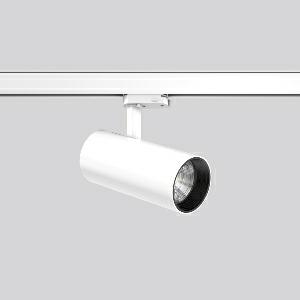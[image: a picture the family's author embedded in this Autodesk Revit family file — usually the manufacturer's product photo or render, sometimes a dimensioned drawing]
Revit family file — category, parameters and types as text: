
# Revit family: deecos_s_mini_742199_002_3_76_5bb7
name_source: partatom
category: Lighting Fixtures
units: mm (PartAtom-declared; Revit-internal decimal feet)

## family parameters
Cut with Voids When Loaded = No
Host = Face
Light Source = No
Part Type = Normal
Room Calculation Point = No
Round Connector Dimension = Use Diameter
Shared = No

## types (1)
- DEECOS S mini (1 x LED Modul 935, 2150 lm, 3500)
    Apparent Load = 20 VA
    Approval mark = CE
    CIE Flux Codes = 96 100 100 100 100
    Color Rendering = 92
    Color Temperature = 3500
    Default Elevation = 1800 mm
    Description = Series: DEECOS S mini
LED surface-mounted projector in modern design with no visible cooling ribs. Housing: die-cast aluminium, powder-coated. Rotation range: 356°. Swivel range: 90°. Black plastic ring and recessed LED to prevent glare from the side. Optical assembly with lens made of plastic (polycarbonate) for the best homogeneous light distribution - can be changed without tools. Best colour rendering index Ra>90. With adapter for RZB 3-circuit DALI tracks. Suitable for Track on ceiling, Wall track. High quality converter without flickering and stroboscopic effect. The following accessories can be mounted without use of tools: interchangeable lenses, decorative glasses, honeycomb louvre, clear and frosted diffusers, white interchangeable plastic ring. 
Colour: traffic white, matt (RAL 9016)
Diameter: 87 mm
Height: 214 mm
Lamp: LED
Socket: without socket
Colour temperature: 3500K
Colour rendering index (CRI): 92
System power: 20 W
Rated luminous flux: 2150 lm
Luminous efficiency: 108 lm/W
Control gear: Converter, dimmable, DALI
Protection class: I
Type of protection: IP 20
    Height = 214 mm
    Lamp = 1 x LED Modul 935
    Lamp Light Flux = 2150 lm
    Lamp count = 1
    Length = 87 mm
    Lifetime = 50000 h
    Luminous efficacy = 108 lm/W
    Manufacturer = RZB
    ModVariant = No
    Model = 742199.002.3.76
    Mounting Place = Ceiling
    Mounting Type = Rail mounted
    Number of Poles = 1
    OnlyDefault = Yes
    Power Factor = 1
    Product Name = DEECOS S mini
    Product group = Track mounted projectors
    ProductGroupID = 301
    Protection Class = Protection class I
    Protection Degree = IP 20
    RLX_Detail_Level = 1
    RLX_Emergency_Light_Flux = 0 lm
    RLX_Emergency_Type = 0
    RLX_Emergency_Type_DB = No
    RlxData = <blob elided: 35045 chars, md5=e0292836>
    Socket = socket
    Standby Power = 0 W
    System Light Flux = 2150 lm
    System Power = 20 W
    Type Comments = Product without accessories
    Type Image = 741930.002.jpg
    URL = http://relux.com
    VarID = ---
    Voltage = 230 V
    Voltage Range = 220-240 V
    Weight = 0.00 kg
    Width = 0 mm  [stored 0 ft]

note: [stored X ft] marks values corroborated as IEEE doubles in the binary element streams (Revit-internal decimal feet)

## geometry (parser evidence)
native form markers: Blend x4, Sweep x12
no freeform markers — native parametric forms only
